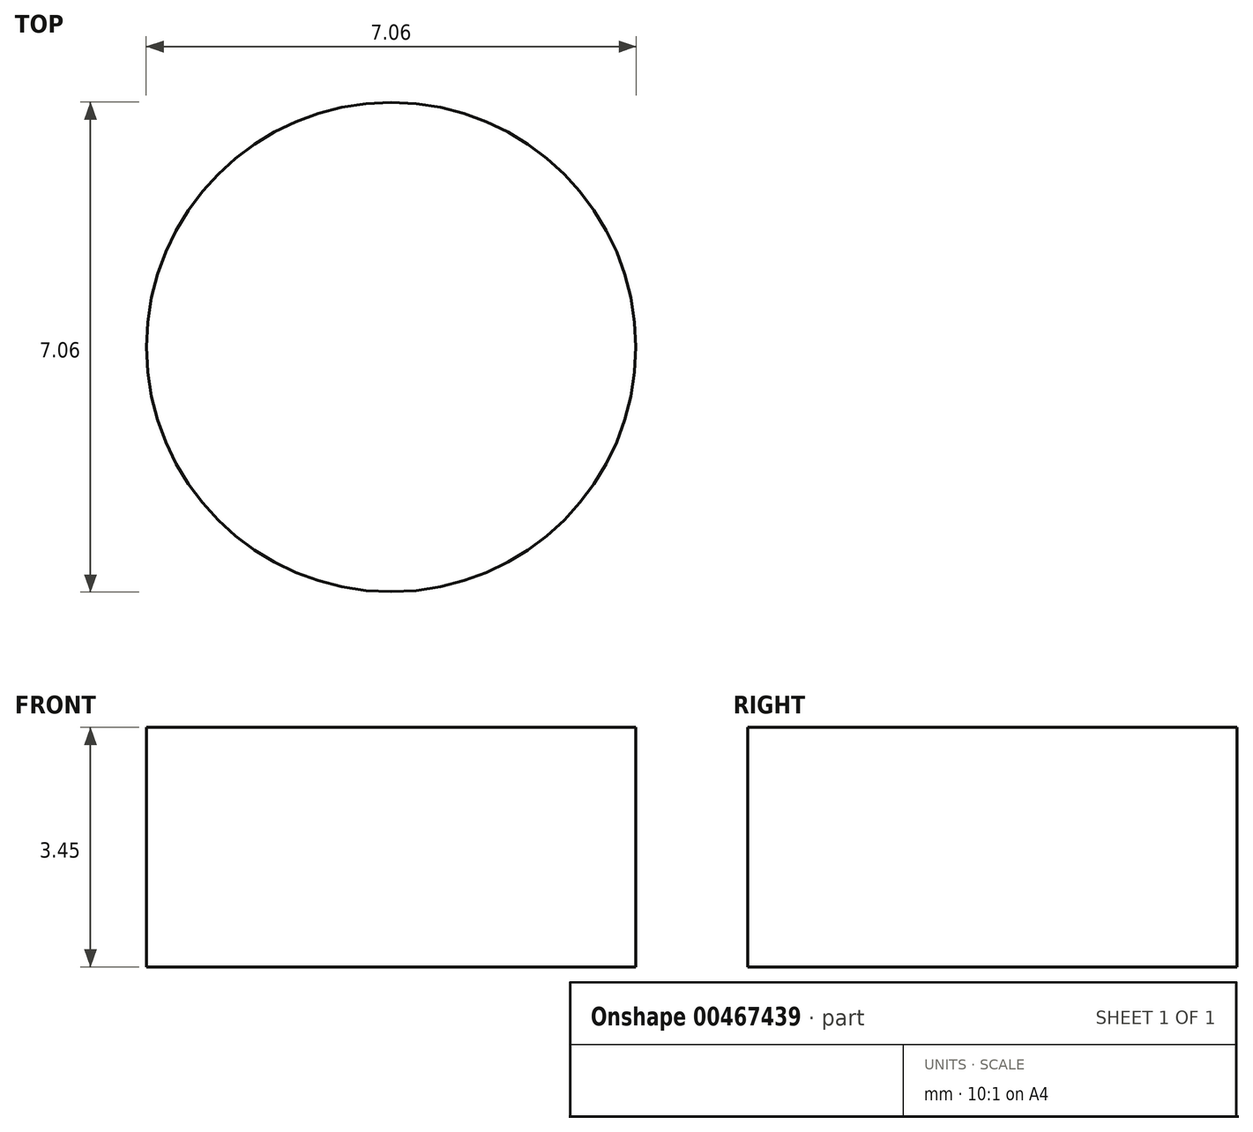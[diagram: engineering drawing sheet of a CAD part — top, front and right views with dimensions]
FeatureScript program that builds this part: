
annotation { "Feature Type Name" : "Feature", "Feature Type Description" : "" }
export const myFeature = defineFeature(function(context is Context, id is Id, definition is map)
    precondition{}
    {
        {
            var Q0;
            Q0=qCreatedBy(makeId("Top.planeOp"),FACE);
            var sketch = newSketch(context, id + "F0", { "sketchPlane" : qUnion([Q0])});
            skCircle(sketch, "E0", {"center": v(0, 0) * mm, "radius": 3.53 * mm});
            skSolve(sketch);
        }
        {
            var Q0;
            Q0=makeQuery(id+"F0.imprint","IMPRINT",FACE,{"disambiguationData":[TD([[makeQuery(id+"F0.imprint","IMPRINT",EDGE,{"derivedFrom":sQuery(id+"F0.wireOp",EDGE,"E0")}),1.0]])]});
            extrude(context, id + "F1", {"entities" : qUnion([Q0]), "depth" : 3.45 * mm});
        }
    });
